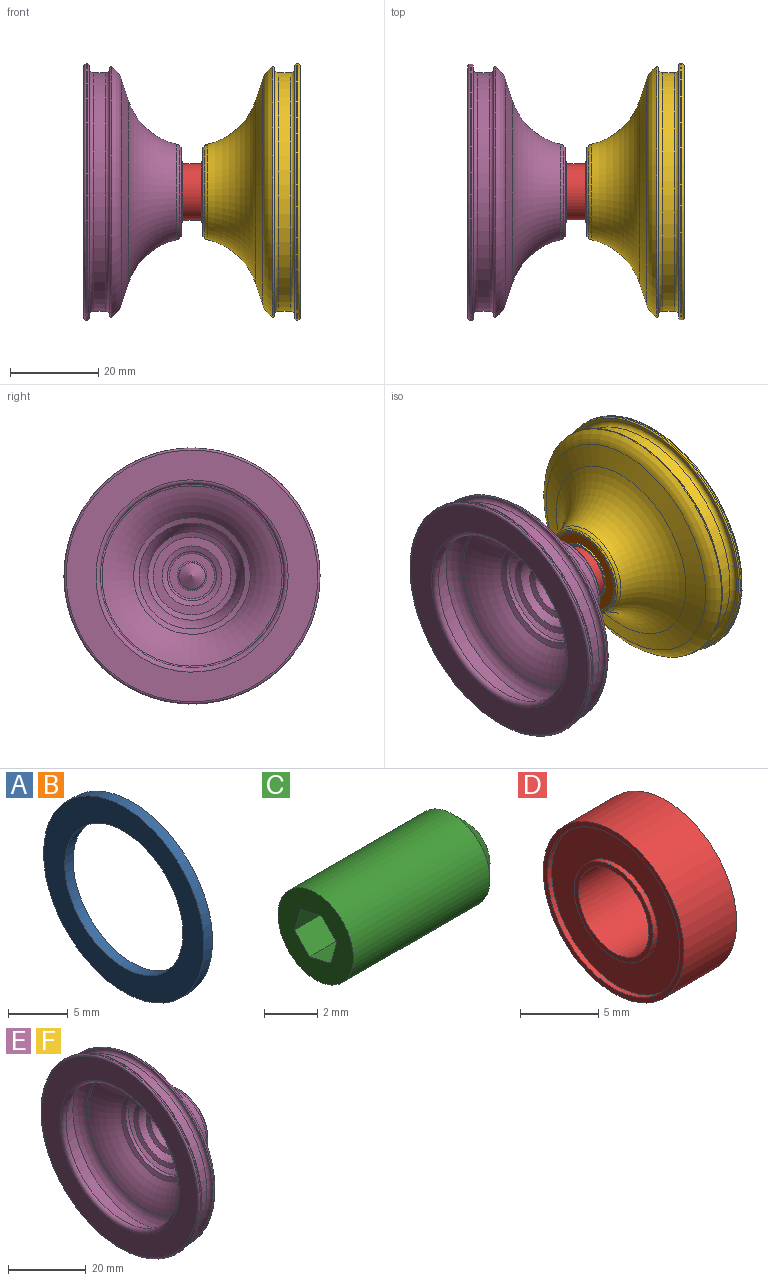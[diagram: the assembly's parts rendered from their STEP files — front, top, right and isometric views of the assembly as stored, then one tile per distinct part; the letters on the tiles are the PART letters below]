
ASSEMBLY  parts=6 mates=5
PART A: 4 faces, bbox 1x19x19 mm
  f0: cylinder r=7mm len=14mm, axis (-1,0,0), area 44mm2, adj f2,f3
  f1: cylinder r=9.5mm len=19mm, axis (-1,0,0), area 59.7mm2, adj f2,f3
  f2: plane 19x19mm, normal (1,0,0), area 129.6mm2, adj f0,f1
  f3: plane 19x19mm, normal (-1,0,0), area 129.6mm2, adj f0,f1
PART B: same geometry as A
PART C: 11 faces, bbox 8x4x4 mm
  f0: plane 4x4mm, normal (-1,0,0), area 9.1mm2, adj f3,f4,f5,f6,f7,f8,f9
  f1: plane 2.5x2.5mm, normal (1,0,0), area 4.9mm2, adj f2
  f2: cone r=2mm half-angle=45deg, axis (-1,0,0), area 10.8mm2, adj f1,f3
  f3: cylinder r=2mm len=7.25mm, axis (-1,0,0), area 91.1mm2, adj f0,f2
  f4: plane 1.5x1.12mm, normal (0,-0.23,-0.97), area 1.7mm2, adj f0,f5,f9,f10
  f5: plane 1.5x1.1mm, normal (0,-0.96,-0.29), area 1.7mm2, adj f0,f4,f6,f10
  f6: plane 1.5x0.84mm, normal (0,-0.73,0.68), area 1.7mm2, adj f0,f5,f7,f10
  f7: plane 1.5x1.12mm, normal (0,0.23,0.97), area 1.7mm2, adj f0,f6,f8,f10
  f8: plane 1.5x1.1mm, normal (0,0.96,0.29), area 1.7mm2, adj f0,f7,f9,f10
  f9: plane 1.5x0.84mm, normal (0,0.73,-0.68), area 1.7mm2, adj f0,f4,f8,f10
  f10: plane 2.24x2.2mm, normal (-1,0,0), area 3.4mm2, adj f4,f5,f6,f7,f8,f9
PART D: 12 faces, bbox 4.8x12.7x12.7 mm
  f0: plane 7.11x7.11mm, normal (-1,0,0), area 8.1mm2, adj f5,f9
  f1: plane 7.11x7.11mm, normal (1,0,0), area 8.1mm2, adj f5,f6
  f2: cylinder r=6.35mm len=12.7mm, axis (-1,0,0), area 189.5mm2, adj f3,f4
  f3: plane 12.7x12.7mm, normal (1,0,0), area 14.7mm2, adj f2,f7
  f4: plane 12.7x12.7mm, normal (-1,0,0), area 14.7mm2, adj f2,f10
  f5: cylinder r=3.17mm len=6.35mm, axis (1,0,0), area 94.8mm2, adj f0,f1
  f6: cylinder r=3.56mm len=7.11mm, axis (1,0,0), area 8.5mm2, adj f1,f8
  f7: cylinder r=5.97mm len=11.94mm, axis (1,0,0), area 14.3mm2, adj f3,f8
  f8: plane 11.94x11.94mm, normal (1,0,0), area 72.2mm2, adj f6,f7
  f9: cylinder r=3.56mm len=7.11mm, axis (-1,0,0), area 8.5mm2, adj f0,f11
  f10: cylinder r=5.97mm len=11.94mm, axis (-1,0,0), area 14.3mm2, adj f4,f11
  f11: plane 11.94x11.94mm, normal (-1,0,0), area 72.2mm2, adj f9,f10
PART E: 58 faces, bbox 24.3x62.8x62.8 mm
  f0: torus R=21.77mm, axis (1,0,0), area 249.1mm2, adj f1,f43
  f1: cone r=20.82mm half-angle=65.2deg, axis (1,0,0), area 198.7mm2, adj f0,f2
  f2: cone r=22.16mm half-angle=17.9deg, axis (1,0,0), area 694.3mm2, adj f1,f3
  f3: torus R=19.31mm, axis (1,0,0), area 515.3mm2, adj f2,f4
  f4: cone r=20.86mm half-angle=71.9deg, axis (-1,0,0), area 63.1mm2, adj f3,f5
  f5: torus R=25.43mm, axis (1,0,0), area 911.3mm2, adj f4,f6
  f6: cone r=12mm half-angle=66.6deg, axis (-1,0,0), area 103.5mm2, adj f5,f7
  f7: cylinder r=12mm len=24mm, axis (1,0,0), area 78.9mm2, adj f6,f8
  f8: torus R=25.43mm, axis (1,0,0), area 315.5mm2, adj f7,f9
  f9: cylinder r=10mm len=20mm, axis (1,0,0), area 271mm2, adj f8,f10
  f10: cone r=8.8mm half-angle=66.6deg, axis (-1,0,0), area 77.2mm2, adj f9,f11
  f11: cylinder r=8.8mm len=17.6mm, axis (1,0,0), area 226.4mm2, adj f10,f12
  f12: plane 17.6x17.6mm, normal (-1,0,0), area 98mm2, adj f11,f13
  f13: cylinder r=6.8mm len=13.6mm, axis (1,0,0), area 137.9mm2, adj f12,f14
  f14: cone r=5.6mm half-angle=66.6deg, axis (-1,0,0), area 50.9mm2, adj f13,f15
  f15: cylinder r=5.6mm len=11.2mm, axis (1,0,0), area 84.8mm2, adj f14,f56
  f16: plane 10.2x10.2mm, normal (-1,0,0), area 45.9mm2, adj f56,f57
  f17: cone r=3.17mm half-angle=45deg, axis (1,0,0), area 1.1mm2, adj f18,f57
  f18: cone r=0mm half-angle=60deg, axis (1,0,0), area 32.3mm2, adj f17
  f19: cone r=2mm half-angle=60deg, axis (1,0,0), area 14.5mm2, adj f20
  f20: cylinder r=2mm len=4mm, axis (1,0,0), area 35.2mm2, adj f19,f21
  f21: plane 5.94x5.94mm, normal (1,0,0), area 15.1mm2, adj f20,f54
  f22: cylinder r=3.17mm len=6.34mm, axis (1,0,0), area 13.9mm2, adj f47,f54
  f23: plane 8.1x8.1mm, normal (1,0,0), area 17.9mm2, adj f47,f48
  f24: cylinder r=4.15mm len=8.3mm, axis (1,0,0), area 20.9mm2, adj f48,f49
  f25: plane 12.7x12.7mm, normal (1,0,0), area 69.9mm2, adj f49,f50
  f26: cylinder r=6.45mm len=12.9mm, axis (1,0,0), area 38.5mm2, adj f50,f51
  f27: plane 13.6x13.6mm, normal (1,0,0), area 10.5mm2, adj f51,f52
  f28: cylinder r=6.9mm len=13.8mm, axis (1,0,0), area 54.2mm2, adj f29,f52
  f29: plane 19.2x19.2mm, normal (1,0,0), area 140mm2, adj f28,f30
  f30: cylinder r=9.6mm len=19.2mm, axis (1,0,0), area 66.4mm2, adj f29,f53
  f31: plane 20.05x20.05mm, normal (1,0,0), area 20.2mm2, adj f46,f53
  f32: torus R=25.43mm, axis (1,0,0), area 1435.4mm2, adj f33,f45
  f33: cone r=25.55mm half-angle=71.9deg, axis (-1,0,0), area 732.4mm2, adj f32,f34
  f34: torus R=24mm, axis (1,0,0), area 632.2mm2, adj f33,f35
  f35: torus R=28.18mm, axis (1,0,0), area 74.1mm2, adj f34,f36
  f36: plane 56.37x56.37mm, normal (-1,0,0), area 32.5mm2, adj f35,f37
  f37: torus R=28mm, axis (1,0,0), area 270.1mm2, adj f36,f38
  f38: cylinder r=27mm len=54mm, axis (1,0,0), area 458mm2, adj f37,f39
  f39: torus R=28mm, axis (1,0,0), area 270.1mm2, adj f38,f40
  f40: plane 57.4x57.4mm, normal (1,0,0), area 124.7mm2, adj f39,f41
  f41: torus R=28.7mm, axis (1,0,0), area 85.5mm2, adj f40,f42
  f42: cylinder r=29mm len=58mm, axis (1,0,0), area 72.9mm2, adj f41,f55
  f43: plane 57x57mm, normal (-1,0,0), area 1062.6mm2, adj f0,f55
  f44: cone r=10.12mm half-angle=38.9deg, axis (-1,0,0), area 26.4mm2, adj f45,f46
  f45: torus R=8.88mm, axis (1,0,0), area 60.2mm2, adj f32,f44
  f46: torus R=10.03mm, axis (1,0,0), area 11.3mm2, adj f31,f44
  f47: torus R=3.27mm, axis (1,0,0), area 3.2mm2, adj f22,f23
  f48: torus R=4.05mm, axis (1,0,0), area 4.1mm2, adj f23,f24
  f49: torus R=4.25mm, axis (1,0,0), area 4.1mm2, adj f24,f25
  f50: torus R=6.35mm, axis (1,0,0), area 6.3mm2, adj f25,f26
  f51: torus R=6.55mm, axis (1,0,0), area 6.4mm2, adj f26,f27
  f52: torus R=6.8mm, axis (1,0,0), area 6.8mm2, adj f27,f28
  f53: torus R=9.7mm, axis (1,0,0), area 9.5mm2, adj f30,f31
  f54: torus R=2.97mm, axis (-1,0,0), area 6.1mm2, adj f21,f22
  f55: torus R=28.5mm, axis (1,0,0), area 142.2mm2, adj f42,f43
  f56: torus R=5.1mm, axis (-1,0,0), area 26.7mm2, adj f15,f16
  f57: torus R=3.38mm, axis (-1,0,0), area 7.9mm2, adj f16,f17
PART F: same geometry as E
PLACE A rot(axis=(-1,0,0),155.4deg) t=(-3.6,0,0)mm
PLACE B rot(axis=(-1,0,0),155.4deg) t=(2.6,0,0)mm
PLACE C rot(axis=(1,0,0),114.6deg) t=(0,0,0)mm
PLACE D rot(axis=(1,0,0),146.7deg) t=(-2.35,0,0)mm
PLACE E rot(axis=(1,0,0),114.6deg) t=(0,0,0)mm
PLACE F rot(axis=(0,-0.54,-0.84),180deg) t=(0,0,0)mm
MATE fastened E.f0 <-> F.f0  axis (1,0,0) through (-2.25,0,0)mm
MATE revolute D.f5 <-> F.f0  axis (1,0,0) through (2.4,0,0)mm
MATE fastened B.f0 <-> F.f0  axis (1,0,0) through (3.6,0,0)mm
MATE fastened A.f0 <-> E.f0  axis (-1,0,0) through (-3.6,0,0)mm
MATE fastened E.f0 <-> C.f2  axis (1,0,0) through (-4.2,0,0)mm
